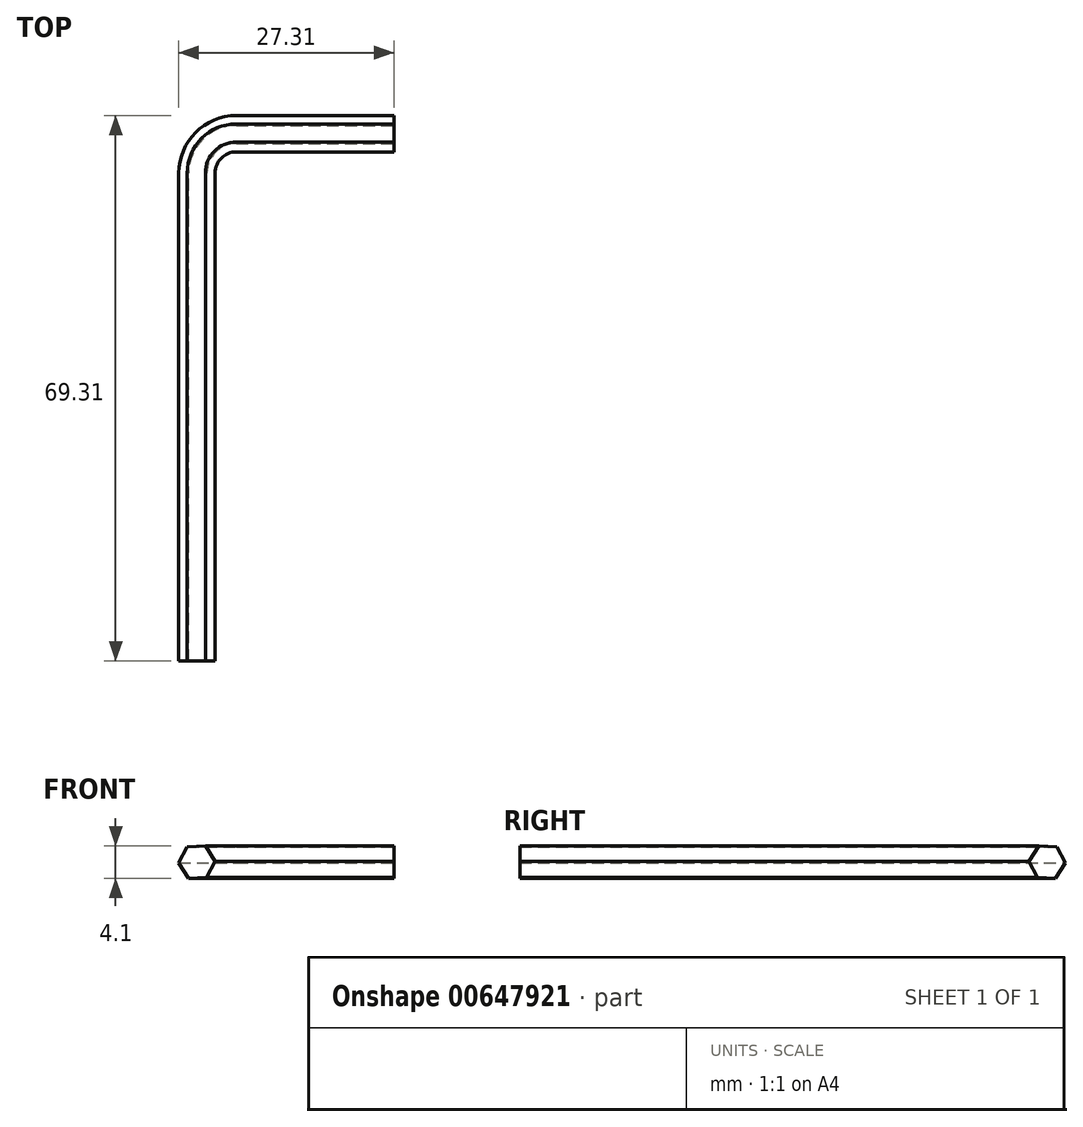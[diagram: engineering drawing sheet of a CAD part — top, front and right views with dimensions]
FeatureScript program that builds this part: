
annotation { "Feature Type Name" : "Feature", "Feature Type Description" : "" }
export const myFeature = defineFeature(function(context is Context, id is Id, definition is map)
    precondition{}
    {
        {
            var Q0;
            Q0=qCreatedBy(makeId("Top.planeOp"),FACE);
            var sketch = newSketch(context, id + "F0", { "sketchPlane" : qUnion([Q0])});
            skLineSegment(sketch, "E0", {"start": v(0, -67) * mm, "end": v(0, -5) * mm});
            skLineSegment(sketch, "E1", {"start": v(5, 0) * mm, "end": v(25, 0) * mm});
            skPoint(sketch, "E2.visualSharp", {"position": v(0, 0) * mm});
            skArc(sketch, "E2.filletArc", {"start": v(5, 0) * mm, "mid": v(1.46, -1.46) * mm, "end": v(0, -5) * mm});
            skSolve(sketch);
        }
        {
            var Q0;
            Q0=sQuery(id+"F0.wireOp",VERTEX,"E0.start");
            var Q1;
            Q1=sQuery(id+"F0.wireOp",EDGE,"E0");
            cPlane(context, id + "F1", {"entities" : qUnion([Q0, Q1]), "cplaneType" : CPlaneType.CURVE_POINT, "offset" : 25 * mm, "width" : 150 * mm, "height" : 150 * mm});
        }
        {
            var Q0;
            Q0=qCreatedBy(id+"F1.planeOp",FACE);
            var sketch = newSketch(context, id + "F2", { "sketchPlane" : qUnion([Q0])});
            skCircle(sketch, "E3.cCircle", {"center": v(0, 0) * mm, "radius": 2 * mm, "construction": true});
            skLineSegment(sketch, "E3.0", {"start": v(-2.3, 0.1) * mm, "end": v(-1.06, 2.05) * mm});
            skLineSegment(sketch, "E3.1", {"start": v(-1.06, 2.05) * mm, "end": v(1.25, 1.94) * mm});
            skLineSegment(sketch, "E3.2", {"start": v(1.25, 1.94) * mm, "end": v(2.3, -0.1) * mm});
            skLineSegment(sketch, "E3.3", {"start": v(2.3, -0.1) * mm, "end": v(1.06, -2.05) * mm});
            skLineSegment(sketch, "E3.4", {"start": v(1.06, -2.05) * mm, "end": v(-1.25, -1.94) * mm});
            skLineSegment(sketch, "E3.5", {"start": v(-1.25, -1.94) * mm, "end": v(-2.3, 0.1) * mm});
            skPoint(sketch, "E3.0.midPoint", {"position": v(-1.68, 1.08) * mm});
            skSolve(sketch);
        }
        {
            var Q0;
            Q0=makeQuery(id+"F2.imprint","IMPRINT",FACE,{"disambiguationData":[TD([[makeQuery(id+"F2.imprint","IMPRINT",EDGE,{"derivedFrom":sQuery(id+"F2.wireOp",EDGE,"E3.0")}),-1.0]])]});
            var Q1;
            Q1=sQuery(id+"F0.wireOp",EDGE,"E0");
            var Q2;
            Q2=sQuery(id+"F0.wireOp",EDGE,"E1");
            var Q3;
            Q3=sQuery(id+"F0.wireOp",EDGE,"E2.filletArc");
            sweep(context, id + "F3", {"profiles" : qUnion([Q0]), "path" : qUnion([Q1, Q2, Q3])});
        }
    });
